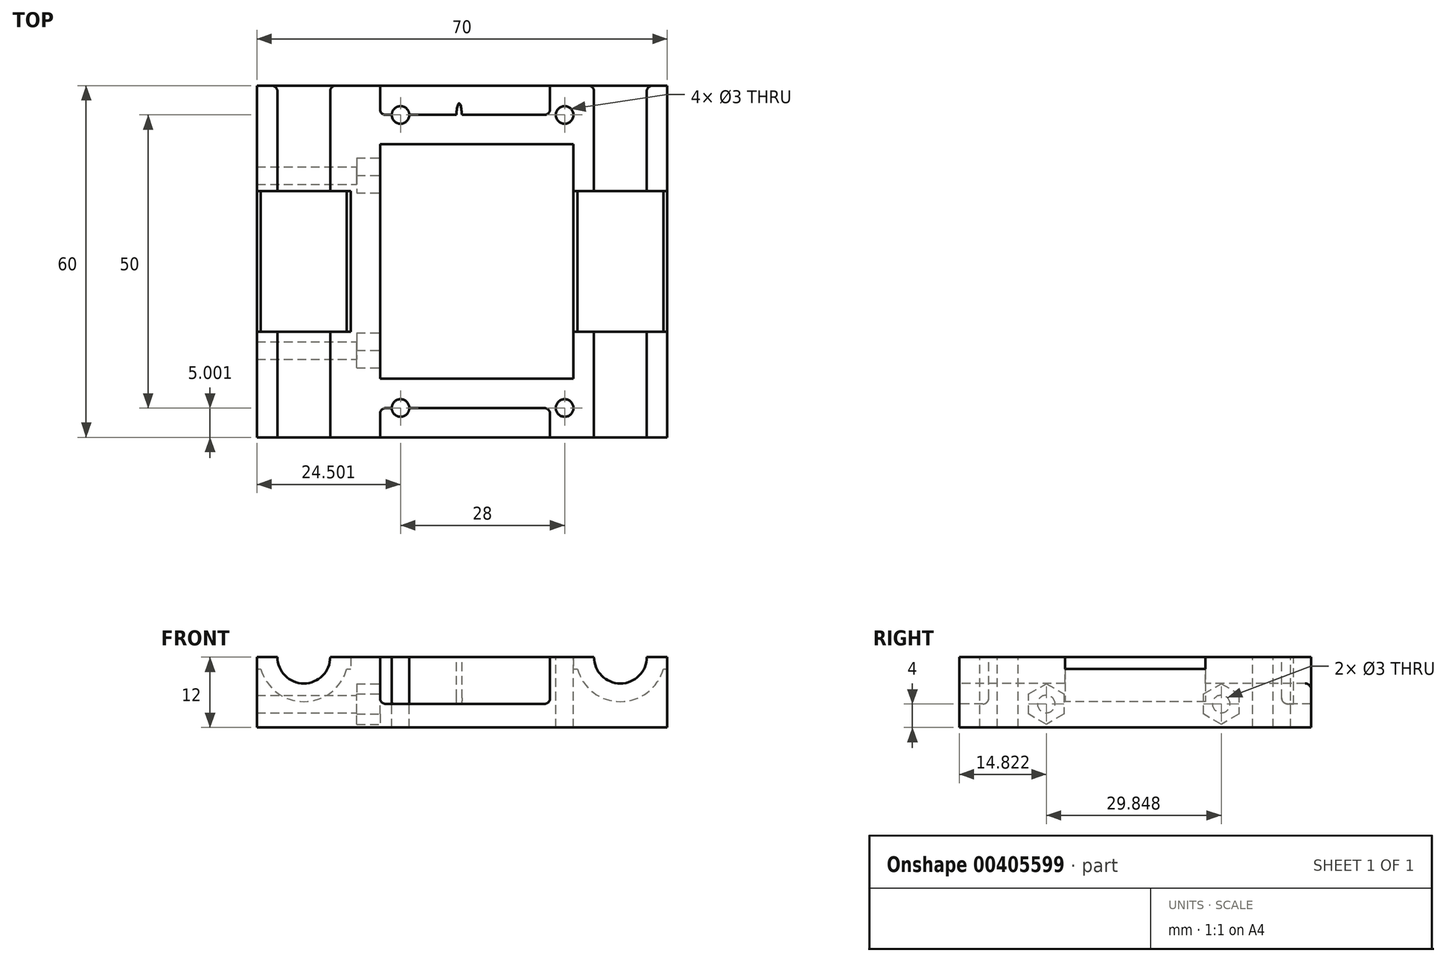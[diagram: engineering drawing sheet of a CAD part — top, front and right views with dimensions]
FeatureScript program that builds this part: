
annotation { "Feature Type Name" : "Feature", "Feature Type Description" : "" }
export const myFeature = defineFeature(function(context is Context, id is Id, definition is map)
    precondition{}
    {
        {
            var Q0;
            Q0=qCreatedBy(makeId("Top.planeOp"),FACE);
            var sketch = newSketch(context, id + "F0", { "sketchPlane" : qUnion([Q0])});
            skLineSegment(sketch, "E0.bottom", {"start": v(-70.16, 26.77) * mm, "end": v(-0.16, 26.77) * mm});
            skLineSegment(sketch, "E0.top", {"start": v(-70.16, -33.23) * mm, "end": v(-0.16, -33.23) * mm});
            skLineSegment(sketch, "E0.left", {"start": v(-70.16, 26.77) * mm, "end": v(-70.16, -33.23) * mm});
            skLineSegment(sketch, "E0.right", {"start": v(-0.16, 26.77) * mm, "end": v(-0.16, -33.23) * mm});
            skSolve(sketch);
        }
        {
            var Q0;
            Q0=qSketchRegion(id+"F0",true);
            extrude(context, id + "F1", {"entities" : qUnion([Q0]), "depth" : 12 * mm});
        }
        {
            var Q0;
            Q0=makeQuery(id+"F1.opExtrude","SWEPT_FACE",FACE,{"disambiguationData":[OSD([sQuery(id+"F0.wireOp",EDGE,"E0.top")])]});
            var sketch = newSketch(context, id + "F2", { "sketchPlane" : qUnion([Q0])});
            skCircle(sketch, "E1", {"center": v(-62.16, 12) * mm, "radius": 7.6 * mm});
            skCircle(sketch, "E2", {"center": v(-8.16, 12) * mm, "radius": 7.6 * mm});
            skLineSegment(sketch, "E3", {"start": v(-72.33, 10) * mm, "end": v(-69.5, 10) * mm});
            skLineSegment(sketch, "E4.trimOffspring", {"start": v(-0.83, 10) * mm, "end": v(3.14, 10) * mm});
            skLineSegment(sketch, "E5", {"start": v(-54.83, 10) * mm, "end": v(-53.13, 10) * mm});
            skLineSegment(sketch, "E6", {"start": v(-53.13, 10) * mm, "end": v(-15.5, 10) * mm});
            skLineSegment(sketch, "E7", {"start": v(-54.16, 12.88) * mm, "end": v(-54.16, 8) * mm});
            skLineSegment(sketch, "E8", {"start": v(-16.16, 15.66) * mm, "end": v(-16.16, -2.6) * mm});
            skCircle(sketch, "E9", {"center": v(-62.16, 12) * mm, "radius": 4.5 * mm});
            skCircle(sketch, "E10", {"center": v(-8.16, 12) * mm, "radius": 4.5 * mm});
            skSolve(sketch);
        }
        {
            var Q0;
            {var subQ0=sQuery(id+"F2.wireOp",EDGE,"E2");var subQ1=makeQuery(id+"F2.imprint","INTERSECT",VERTEX,{"derivedFrom":[subQ0,sQuery(id+"F2.wireOp",EDGE,"E4.trimOffspring")]});Q0=makeQuery(id+"F2.imprint","IMPRINT",FACE,{"disambiguationData":[TD([[makeQuery(id+"F2.imprint","IMPRINT",EDGE,{"disambiguationData":[TD([[subQ1,1.0]])],"derivedFrom":subQ0}),1.0]])]});}
            var Q1;
            {var subQ0=sQuery(id+"F2.wireOp",EDGE,"E1");var subQ1=makeQuery(id+"F2.imprint","INTERSECT",VERTEX,{"derivedFrom":[subQ0,sQuery(id+"F2.wireOp",EDGE,"E3")]});Q1=makeQuery(id+"F2.imprint","IMPRINT",FACE,{"disambiguationData":[TD([[makeQuery(id+"F2.imprint","IMPRINT",EDGE,{"disambiguationData":[TD([[subQ1,1.0]])],"derivedFrom":subQ0}),1.0]])]});}
            var Q2;
            {var subQ0=sQuery(id+"F2.wireOp",EDGE,"E4.trimOffspring");var subQ1=sQuery(id+"F2.wireOp",EDGE,"E2");var subQ2=makeQuery(id+"F2.imprint","INTERSECT",VERTEX,{"derivedFrom":[subQ1,subQ0]});Q2=makeQuery(id+"F2.imprint","IMPRINT",FACE,{"disambiguationData":[TD([[makeQuery(id+"F2.imprint","IMPRINT",EDGE,{"disambiguationData":[TD([[subQ2,-1.0]])],"derivedFrom":subQ1}),-1.0]])]});}
            var Q3;
            {var subQ0=sQuery(id+"F2.wireOp",EDGE,"E3");var subQ1=sQuery(id+"F2.wireOp",EDGE,"E1");var subQ2=makeQuery(id+"F2.imprint","INTERSECT",VERTEX,{"derivedFrom":[subQ1,subQ0]});Q3=makeQuery(id+"F2.imprint","IMPRINT",FACE,{"disambiguationData":[TD([[makeQuery(id+"F2.imprint","IMPRINT",EDGE,{"disambiguationData":[TD([[subQ2,1.0]])],"derivedFrom":subQ1}),-1.0]])]});}
            var Q4;
            {var subQ0=sQuery(id+"F2.wireOp",EDGE,"E6");var subQ1=sQuery(id+"F2.wireOp",EDGE,"E2");var subQ2=makeQuery(id+"F2.imprint","INTERSECT",VERTEX,{"derivedFrom":[subQ1,subQ0]});Q4=makeQuery(id+"F2.imprint","IMPRINT",FACE,{"disambiguationData":[TD([[makeQuery(id+"F2.imprint","IMPRINT",EDGE,{"disambiguationData":[TD([[subQ2,1.0]])],"derivedFrom":subQ1}),-1.0]])]});}
            var Q5;
            {var subQ0=sQuery(id+"F2.wireOp",EDGE,"E5");var subQ1=sQuery(id+"F2.wireOp",EDGE,"E1");var subQ2=makeQuery(id+"F2.imprint","INTERSECT",VERTEX,{"derivedFrom":[subQ1,subQ0]});Q5=makeQuery(id+"F2.imprint","IMPRINT",FACE,{"disambiguationData":[TD([[makeQuery(id+"F2.imprint","IMPRINT",EDGE,{"disambiguationData":[TD([[subQ2,-1.0]])],"derivedFrom":subQ1}),-1.0]])]});}
            extrude(context, id + "F3", {"entities" : qUnion([Q0, Q1, Q2, Q3, Q4, Q5]), "operationType" : NewBodyOperationType.REMOVE, "oppositeDirection" : true, "depth" : 42 * mm});
        }
        {
            var Q0;
            {var subQ0=sQuery(id+"F2.wireOp",EDGE,"E3");var subQ1=sQuery(id+"F2.wireOp",EDGE,"E1");var subQ2=makeQuery(id+"F2.imprint","INTERSECT",VERTEX,{"derivedFrom":[subQ1,subQ0]});Q0=makeQuery(id+"F2.imprint","IMPRINT",FACE,{"disambiguationData":[TD([[makeQuery(id+"F2.imprint","IMPRINT",EDGE,{"disambiguationData":[TD([[subQ2,1.0]])],"derivedFrom":subQ1}),-1.0]])]});}
            var Q1;
            {var subQ0=sQuery(id+"F2.wireOp",EDGE,"E1");var subQ1=makeQuery(id+"F2.imprint","INTERSECT",VERTEX,{"derivedFrom":[subQ0,sQuery(id+"F2.wireOp",EDGE,"E3")]});Q1=makeQuery(id+"F2.imprint","IMPRINT",FACE,{"disambiguationData":[TD([[makeQuery(id+"F2.imprint","IMPRINT",EDGE,{"disambiguationData":[TD([[subQ1,1.0]])],"derivedFrom":subQ0}),1.0]])]});}
            var Q2;
            {var subQ0=sQuery(id+"F2.wireOp",EDGE,"E4.trimOffspring");var subQ1=sQuery(id+"F2.wireOp",EDGE,"E2");var subQ2=makeQuery(id+"F2.imprint","INTERSECT",VERTEX,{"derivedFrom":[subQ1,subQ0]});Q2=makeQuery(id+"F2.imprint","IMPRINT",FACE,{"disambiguationData":[TD([[makeQuery(id+"F2.imprint","IMPRINT",EDGE,{"disambiguationData":[TD([[subQ2,-1.0]])],"derivedFrom":subQ1}),-1.0]])]});}
            var Q3;
            {var subQ0=sQuery(id+"F2.wireOp",EDGE,"E5");var subQ1=sQuery(id+"F2.wireOp",EDGE,"E1");var subQ2=makeQuery(id+"F2.imprint","INTERSECT",VERTEX,{"derivedFrom":[subQ1,subQ0]});Q3=makeQuery(id+"F2.imprint","IMPRINT",FACE,{"disambiguationData":[TD([[makeQuery(id+"F2.imprint","IMPRINT",EDGE,{"disambiguationData":[TD([[subQ2,-1.0]])],"derivedFrom":subQ1}),-1.0]])]});}
            var Q4;
            {var subQ0=sQuery(id+"F2.wireOp",EDGE,"E2");var subQ1=makeQuery(id+"F2.imprint","INTERSECT",VERTEX,{"derivedFrom":[subQ0,sQuery(id+"F2.wireOp",EDGE,"E6")]});Q4=makeQuery(id+"F2.imprint","IMPRINT",FACE,{"disambiguationData":[TD([[makeQuery(id+"F2.imprint","IMPRINT",EDGE,{"disambiguationData":[TD([[subQ1,1.0]])],"derivedFrom":subQ0}),1.0]])]});}
            var Q5;
            {var subQ0=sQuery(id+"F2.wireOp",EDGE,"E6");var subQ1=sQuery(id+"F2.wireOp",EDGE,"E2");var subQ2=makeQuery(id+"F2.imprint","INTERSECT",VERTEX,{"derivedFrom":[subQ1,subQ0]});Q5=makeQuery(id+"F2.imprint","IMPRINT",FACE,{"disambiguationData":[TD([[makeQuery(id+"F2.imprint","IMPRINT",EDGE,{"disambiguationData":[TD([[subQ2,1.0]])],"derivedFrom":subQ1}),-1.0]])]});}
            extrude(context, id + "F4", {"entities" : qUnion([Q0, Q1, Q2, Q3, Q4, Q5]), "operationType" : NewBodyOperationType.ADD, "oppositeDirection" : true, "depth" : 18 * mm});
        }
        {
            var Q0;
            {var subQ0=sQuery(id+"F2.wireOp",EDGE,"E2");var subQ1=sQuery(id+"F0.wireOp",EDGE,"E0.top");var subQ2=makeQuery(id+"F1.opExtrude","CAP_EDGE",EDGE,{"disambiguationData":[OSD([subQ1])],"isStart":false});var subQ3=makeQuery(id+"F2.imprint","INTERSECT",VERTEX,{"disambiguationData":[OD(1.0)],"derivedFrom":[subQ2,subQ0]});var subQ4=sQuery(id+"F0.wireOp",EDGE,"E0.right");var subQ5=sQuery(id+"F2.wireOp",EDGE,"E1");var subQ6=makeQuery(id+"F2.imprint","INTERSECT",VERTEX,{"disambiguationData":[OD(0.0)],"derivedFrom":[subQ2,subQ5]});var subQ7=sQuery(id+"F0.wireOp",EDGE,"E0.left");Q0=makeQuery(id+"F4.boolean.opBoolean","MERGE",FACE,{"derivedFrom":[makeQuery(id+"F1.opExtrude","CAP_FACE",FACE,{"disambiguationData":[OSD([sQuery(id+"F0.wireOp",EDGE,"E0.bottom"),subQ1,subQ7,subQ4])],"isStart":false}),makeQuery(id+"F4.opExtrude","SWEPT_FACE",FACE,{"disambiguationData":[OSD([subQ1]),TDD([makeQuery(id+"F2.imprint","IMPRINT",EDGE,{"disambiguationData":[TD([[subQ6,1.0]])],"derivedFrom":subQ2}),makeQuery(id+"F2.imprint","IMPRINT",EDGE,{"disambiguationData":[TD([[subQ6,-1.0]])],"derivedFrom":subQ2})])]}),makeQuery(id+"F4.opExtrude","SWEPT_FACE",FACE,{"disambiguationData":[OSD([subQ1]),TDD([makeQuery(id+"F2.imprint","IMPRINT",EDGE,{"disambiguationData":[TD([[subQ3,-1.0]])],"derivedFrom":subQ2}),makeQuery(id+"F2.imprint","IMPRINT",EDGE,{"disambiguationData":[TD([[makeQuery(id+"F2.imprint","INTERSECT",VERTEX,{"disambiguationData":[OD(0.0)],"derivedFrom":[subQ2,subQ0]}),-1.0]])],"derivedFrom":subQ2})])]})]});}
            var sketch = newSketch(context, id + "F5", { "sketchPlane" : qUnion([Q0])});
            skLineSegment(sketch, "E11.bottom", {"start": v(-16.16, -23.23) * mm, "end": v(-49.16, -23.23) * mm});
            skLineSegment(sketch, "E11.top", {"start": v(-16.16, 16.77) * mm, "end": v(-49.16, 16.77) * mm});
            skLineSegment(sketch, "E11.left", {"start": v(-16.16, -23.23) * mm, "end": v(-16.16, 16.77) * mm});
            skPoint(sketch, "E11.middle", {"position": v(-35.16, -3.23) * mm});
            skPoint(sketch, "E11.middle.positionSnap0", {"position": v(-35.16, -33.23) * mm});
            skPoint(sketch, "E11.centerSnap0", {"position": v(-35.16, -33.23) * mm});
            skCircle(sketch, "E12", {"center": v(-45.16, 21.77) * mm, "radius": 1.77 * mm});
            skCircle(sketch, "E13", {"center": v(-17.16, 21.77) * mm, "radius": 1.92 * mm});
            skCircle(sketch, "E14", {"center": v(-45.16, -28.23) * mm, "radius": 1.72 * mm});
            skCircle(sketch, "E15", {"center": v(-17.16, -28.23) * mm, "radius": 1.92 * mm});
            skLineSegment(sketch, "E16.right", {"start": v(-49.16, 26.77) * mm, "end": v(-49.16, -33.23) * mm});
            skLineSegment(sketch, "E17", {"start": v(-55.16, 26.77) * mm, "end": v(-55.16, -33.23) * mm});
            skLineSegment(sketch, "E18", {"start": v(-50.16, 26.77) * mm, "end": v(-50.16, -33.23) * mm});
            skSolve(sketch);
        }
        {
            var Q0;
            Q0=makeQuery(id+"F5.imprint","IMPRINT",FACE,{"disambiguationData":[TD([[makeQuery(id+"F5.imprint","IMPRINT",EDGE,{"derivedFrom":sQuery(id+"F5.wireOp",EDGE,"E11.bottom")}),-1.0]])]});
            extrude(context, id + "F6", {"entities" : qUnion([Q0]), "operationType" : NewBodyOperationType.REMOVE, "oppositeDirection" : true, "depth" : 25 * mm});
        }
        {
            var Q0;
            {var subQ0=sQuery(id+"F2.wireOp",EDGE,"E9");var subQ1=makeQuery(id+"F1.opExtrude","CAP_EDGE",EDGE,{"disambiguationData":[OSD([sQuery(id+"F0.wireOp",EDGE,"E0.top")])],"isStart":false});var subQ2=makeQuery(id+"F2.imprint","INTERSECT",VERTEX,{"disambiguationData":[OD(0.0)],"derivedFrom":[subQ1,subQ0]});Q0=makeQuery(id+"F2.imprint","IMPRINT",FACE,{"disambiguationData":[TD([[makeQuery(id+"F2.imprint","IMPRINT",EDGE,{"disambiguationData":[TD([[subQ2,1.0]])],"derivedFrom":subQ0}),1.0]])]});}
            var Q1;
            {var subQ0=sQuery(id+"F2.wireOp",EDGE,"E9");var subQ1=makeQuery(id+"F1.opExtrude","CAP_EDGE",EDGE,{"disambiguationData":[OSD([sQuery(id+"F0.wireOp",EDGE,"E0.top")])],"isStart":false});var subQ2=makeQuery(id+"F2.imprint","INTERSECT",VERTEX,{"disambiguationData":[OD(0.0)],"derivedFrom":[subQ1,subQ0]});Q1=makeQuery(id+"F2.imprint","IMPRINT",FACE,{"disambiguationData":[TD([[makeQuery(id+"F2.imprint","IMPRINT",EDGE,{"disambiguationData":[TD([[subQ2,-1.0]])],"derivedFrom":subQ0}),1.0]])]});}
            var Q2;
            {var subQ0=sQuery(id+"F2.wireOp",EDGE,"E10");var subQ1=makeQuery(id+"F1.opExtrude","CAP_EDGE",EDGE,{"disambiguationData":[OSD([sQuery(id+"F0.wireOp",EDGE,"E0.top")])],"isStart":false});var subQ2=makeQuery(id+"F2.imprint","INTERSECT",VERTEX,{"disambiguationData":[OD(0.0)],"derivedFrom":[subQ1,subQ0]});Q2=makeQuery(id+"F2.imprint","IMPRINT",FACE,{"disambiguationData":[TD([[makeQuery(id+"F2.imprint","IMPRINT",EDGE,{"disambiguationData":[TD([[subQ2,1.0]])],"derivedFrom":subQ0}),1.0]])]});}
            var Q3;
            {var subQ0=sQuery(id+"F2.wireOp",EDGE,"E10");var subQ1=makeQuery(id+"F1.opExtrude","CAP_EDGE",EDGE,{"disambiguationData":[OSD([sQuery(id+"F0.wireOp",EDGE,"E0.top")])],"isStart":false});var subQ2=makeQuery(id+"F2.imprint","INTERSECT",VERTEX,{"disambiguationData":[OD(0.0)],"derivedFrom":[subQ1,subQ0]});Q3=makeQuery(id+"F2.imprint","IMPRINT",FACE,{"disambiguationData":[TD([[makeQuery(id+"F2.imprint","IMPRINT",EDGE,{"disambiguationData":[TD([[subQ2,-1.0]])],"derivedFrom":subQ0}),1.0]])]});}
            extrude(context, id + "F7", {"entities" : qUnion([Q0, Q1, Q2, Q3]), "operationType" : NewBodyOperationType.REMOVE, "endBound" : BoundingType.THROUGH_ALL, "oppositeDirection" : true, "depth" : 25 * mm});
        }
        {
            var Q0;
            {var subQ0=sQuery(id+"F2.wireOp",EDGE,"E10");var subQ1=sQuery(id+"F2.wireOp",EDGE,"E8");var subQ2=sQuery(id+"F2.wireOp",EDGE,"E6");var subQ3=sQuery(id+"F2.wireOp",EDGE,"E4.trimOffspring");var subQ4=sQuery(id+"F2.wireOp",EDGE,"E2");var subQ5=sQuery(id+"F0.wireOp",EDGE,"E0.right");var subQ6=sQuery(id+"F0.wireOp",EDGE,"E0.top");var subQ7=makeQuery(id+"F4.opExtrude","CAP_FACE",FACE,{"disambiguationData":[OSD([subQ6,subQ5,subQ4,subQ3,subQ2,subQ1,subQ0])],"isStart":false});var subQ8=makeQuery(id+"F1.opExtrude","SWEPT_FACE",FACE,{"disambiguationData":[OSD([subQ6])]});var subQ9=makeQuery(id+"F4.opExtrude","CAP_FACE",FACE,{"disambiguationData":[OSD([subQ6,subQ5,subQ4,subQ3,subQ2,subQ1,subQ0])],"isStart":true});var subQ10=sQuery(id+"F0.wireOp",EDGE,"E0.left");var subQ11=makeQuery(id+"F1.opExtrude","CAP_FACE",FACE,{"disambiguationData":[OSD([sQuery(id+"F0.wireOp",EDGE,"E0.bottom"),subQ6,subQ10,subQ5])],"isStart":false});var subQ12=sQuery(id+"F2.wireOp",EDGE,"E9");var subQ13=sQuery(id+"F2.wireOp",EDGE,"E7");var subQ14=sQuery(id+"F2.wireOp",EDGE,"E5");var subQ15=sQuery(id+"F2.wireOp",EDGE,"E3");var subQ16=sQuery(id+"F2.wireOp",EDGE,"E1");var subQ17=makeQuery(id+"F4.opExtrude","CAP_FACE",FACE,{"disambiguationData":[OSD([subQ6,subQ10,subQ16,subQ15,subQ14,subQ13,subQ12])],"isStart":true});var subQ18=makeQuery(id+"F1.opExtrude","CAP_EDGE",EDGE,{"disambiguationData":[OSD([subQ6])],"isStart":false});var subQ19=makeQuery(id+"F2.imprint","INTERSECT",VERTEX,{"disambiguationData":[OD(0.0)],"derivedFrom":[subQ18,subQ16]});var subQ20=makeQuery(id+"F2.imprint","IMPRINT",EDGE,{"disambiguationData":[TD([[subQ19,-1.0]])],"derivedFrom":subQ18});var subQ21=makeQuery(id+"F2.imprint","IMPRINT",EDGE,{"disambiguationData":[TD([[subQ19,1.0]])],"derivedFrom":subQ18});var subQ22=makeQuery(id+"F4.opExtrude","SWEPT_FACE",FACE,{"disambiguationData":[OSD([subQ6]),TDD([subQ21,subQ20])]});var subQ23=makeQuery(id+"F2.imprint","INTERSECT",VERTEX,{"disambiguationData":[OD(1.0)],"derivedFrom":[subQ18,subQ4]});var subQ24=makeQuery(id+"F2.imprint","IMPRINT",EDGE,{"disambiguationData":[TD([[subQ23,1.0]])],"derivedFrom":subQ18});var subQ25=makeQuery(id+"F2.imprint","IMPRINT",EDGE,{"disambiguationData":[TD([[subQ23,-1.0]])],"derivedFrom":subQ18});var subQ26=makeQuery(id+"F4.opExtrude","SWEPT_FACE",FACE,{"disambiguationData":[OSD([subQ6]),TDD([subQ25,subQ24])]});var subQ27=makeQuery(id+"F2.imprint","INTERSECT",VERTEX,{"disambiguationData":[OD(1.0)],"derivedFrom":[subQ18,subQ16]});var subQ28=makeQuery(id+"F2.imprint","IMPRINT",EDGE,{"disambiguationData":[TD([[subQ27,1.0]])],"derivedFrom":subQ18});var subQ29=makeQuery(id+"F2.imprint","IMPRINT",EDGE,{"disambiguationData":[TD([[makeQuery(id+"F2.imprint","INTERSECT",VERTEX,{"derivedFrom":[subQ18,subQ13]}),1.0]])],"derivedFrom":subQ18});var subQ30=makeQuery(id+"F4.opExtrude","SWEPT_FACE",FACE,{"disambiguationData":[OSD([subQ6]),TDD([subQ29,subQ28])]});var subQ31=makeQuery(id+"F2.imprint","INTERSECT",VERTEX,{"disambiguationData":[OD(0.0)],"derivedFrom":[subQ18,subQ4]});var subQ32=makeQuery(id+"F2.imprint","IMPRINT",EDGE,{"disambiguationData":[TD([[subQ31,-1.0]])],"derivedFrom":subQ18});var subQ33=makeQuery(id+"F2.imprint","IMPRINT",EDGE,{"disambiguationData":[TD([[makeQuery(id+"F2.imprint","INTERSECT",VERTEX,{"derivedFrom":[subQ18,subQ1]}),-1.0]])],"derivedFrom":subQ18});var subQ34=makeQuery(id+"F4.opExtrude","SWEPT_FACE",FACE,{"disambiguationData":[OSD([subQ6]),TDD([subQ33,subQ32])]});var subQ35=makeQuery(id+"F7.opExtrude","SWEPT_FACE",FACE,{"disambiguationData":[OSD([subQ0])]});var subQ36=sQuery(id+"F5.wireOp",EDGE,"E11.bottom");var subQ37=makeQuery(id+"F6.boolean.opBoolean","COPY",FACE,{"derivedFrom":makeQuery(id+"F6.opExtrude","SWEPT_FACE",FACE,{"disambiguationData":[OSD([subQ36])]})});var subQ38=makeQuery(id+"F6.boolean.opBoolean","COPY",FACE,{"derivedFrom":makeQuery(id+"F6.opExtrude","SWEPT_FACE",FACE,{"disambiguationData":[OSD([sQuery(id+"F5.wireOp",EDGE,"E11.left")])]})});Q0=makeQuery(id+"FtBxvbWRXRIYLMa_1.boolean.opBoolean","SPLIT",FACE,{"disambiguationData":[TD([subQ37])],"derivedFrom":makeQuery(id+"F7.boolean.opBoolean","SPLIT",FACE,{"disambiguationData":[TD([subQ8,subQ17,makeQuery(id+"F4.opExtrude","CAP_FACE",FACE,{"disambiguationData":[OSD([subQ6,subQ10,subQ16,subQ15,subQ14,subQ13,subQ12])],"isStart":false}),subQ9,subQ7,subQ37,subQ38,makeQuery(id+"F6.boolean.opBoolean","COPY",FACE,{"derivedFrom":makeQuery(id+"F6.opExtrude","SWEPT_FACE",FACE,{"disambiguationData":[OSD([sQuery(id+"F5.wireOp",EDGE,"E16.left")])]})}),makeQuery(id+"F7.opExtrude","SWEPT_FACE",FACE,{"disambiguationData":[OSD([subQ12])]}),subQ35])],"derivedFrom":makeQuery(id+"F4.boolean.opBoolean","MERGE",FACE,{"derivedFrom":[subQ11,subQ22,subQ26,subQ30,subQ34]})})});}
            var sketch = newSketch(context, id + "F8", { "sketchPlane" : qUnion([Q0])});
            skLineSegment(sketch, "E19.bottom", {"start": v(-40.16, -27.23) * mm, "end": v(-26.16, -27.23) * mm});
            skLineSegment(sketch, "E19.top", {"start": v(-40.16, -33.23) * mm, "end": v(-26.16, -33.23) * mm});
            skLineSegment(sketch, "E20", {"start": v(-40.16, -27.23) * mm, "end": v(-40.16, -27.23) * mm});
            skLineSegment(sketch, "E21", {"start": v(-38.16, -27.23) * mm, "end": v(-37.16, -27.23) * mm});
            skLineSegment(sketch, "E22", {"start": v(-36.16, -27.23) * mm, "end": v(-35.16, -27.23) * mm});
            skLineSegment(sketch, "E23", {"start": v(-35.16, -27.23) * mm, "end": v(-34.16, -27.23) * mm});
            skLineSegment(sketch, "E24", {"start": v(-33.16, -27.23) * mm, "end": v(-32.16, -27.23) * mm});
            skLineSegment(sketch, "E25", {"start": v(-31.16, -27.23) * mm, "end": v(-30.16, -27.23) * mm});
            skLineSegment(sketch, "E26", {"start": v(-29.16, -27.23) * mm, "end": v(-28.16, -27.23) * mm});
            skLineSegment(sketch, "E27", {"start": v(-27.16, -27.23) * mm, "end": v(-26.16, -27.23) * mm});
            skLineSegment(sketch, "E28", {"start": v(-40.13, -28.23) * mm, "end": v(-27.19, -28.23) * mm});
            skLineSegment(sketch, "E29", {"start": v(-40.16, -23.23) * mm, "end": v(-40.16, -27.23) * mm});
            skLineSegment(sketch, "E30.trimOffspring", {"start": v(-40.16, -31.23) * mm, "end": v(-40.16, -33.23) * mm});
            skLineSegment(sketch, "E31", {"start": v(-40.16, -31.23) * mm, "end": v(-26.16, -31.23) * mm});
            skLineSegment(sketch, "E32.top", {"start": v(-26.16, -27.23) * mm, "end": v(-20.16, -27.23) * mm});
            skLineSegment(sketch, "E33.trimOffspring", {"start": v(-26.16, -31.23) * mm, "end": v(-26.16, -33.23) * mm});
            skLineSegment(sketch, "E34", {"start": v(-16.16, -23.23) * mm, "end": v(-16.16, 16.77) * mm});
            skPoint(sketch, "E34.endSnap0", {"position": v(-16.16, -19.23) * mm});
            skLineSegment(sketch, "E35", {"start": v(-16.16, -3.23) * mm, "end": v(-49.15, -3.23) * mm});
            skLineSegment(sketch, "E36.MirrorCS", {"start": v(-16.16, 16.77) * mm, "end": v(-16.16, -23.23) * mm});
            skPoint(sketch, "E37.MirrorP", {"position": v(-16.16, 12.77) * mm});
            skLineSegment(sketch, "E38.MirrorCS", {"start": v(-36.16, 20.77) * mm, "end": v(-35.16, 20.77) * mm});
            skLineSegment(sketch, "E39.MirrorCS", {"start": v(-35.16, 20.77) * mm, "end": v(-34.16, 20.77) * mm});
            skLineSegment(sketch, "E40.MirrorCS", {"start": v(-38.16, 20.77) * mm, "end": v(-37.16, 20.77) * mm});
            skLineSegment(sketch, "E41.MirrorCS", {"start": v(-29.16, 20.77) * mm, "end": v(-28.16, 20.77) * mm});
            skLineSegment(sketch, "E42.MirrorCS", {"start": v(-40.16, 24.77) * mm, "end": v(-40.16, 26.77) * mm});
            skLineSegment(sketch, "E43.MirrorCS", {"start": v(-31.16, 20.77) * mm, "end": v(-30.16, 20.77) * mm});
            skLineSegment(sketch, "E44.MirrorCS", {"start": v(-27.16, 20.77) * mm, "end": v(-26.16, 20.77) * mm});
            skLineSegment(sketch, "E45.MirrorCS", {"start": v(-40.16, 20.77) * mm, "end": v(-26.16, 20.77) * mm});
            skLineSegment(sketch, "E46.MirrorCS", {"start": v(-40.13, 21.77) * mm, "end": v(-27.19, 21.77) * mm});
            skEllipticalArc(sketch, "E47.MirrorCS", {});
            skLineSegment(sketch, "E48.MirrorCS", {"start": v(-33.16, 20.77) * mm, "end": v(-32.16, 20.77) * mm});
            skEllipticalArc(sketch, "E49.MirrorCS", {});
            skLineSegment(sketch, "E50.MirrorCS", {"start": v(-26.16, 24.77) * mm, "end": v(-26.16, 26.77) * mm});
            skLineSegment(sketch, "E51.MirrorCS", {"start": v(-40.16, 24.77) * mm, "end": v(-26.16, 24.77) * mm});
            skLineSegment(sketch, "E52.MirrorCS", {"start": v(-40.16, 26.77) * mm, "end": v(-26.16, 26.77) * mm});
            skEllipticalArc(sketch, "E53.MirrorCS", {});
            skLineSegment(sketch, "E54.MirrorCS", {"start": v(-26.16, 20.77) * mm, "end": v(-17.16, 20.77) * mm});
            skLineSegment(sketch, "E55.MirrorCS", {"start": v(-40.16, 16.77) * mm, "end": v(-40.16, 20.77) * mm});
            skEllipticalArc(sketch, "E56.MirrorCS", {});
            skEllipticalArc(sketch, "E57.MirrorCS", {});
            skEllipticalArc(sketch, "E58.MirrorCS", {});
            skEllipticalArc(sketch, "E59.MirrorCS", {});
            skLineSegment(sketch, "E60", {"start": v(-40.16, 26.77) * mm, "end": v(-49.16, 26.77) * mm});
            skLineSegment(sketch, "E61", {"start": v(-49.16, 26.77) * mm, "end": v(-49.16, 16.77) * mm});
            skLineSegment(sketch, "E62", {"start": v(-49.16, 16.77) * mm, "end": v(-40.16, 16.77) * mm});
            skLineSegment(sketch, "E63", {"start": v(-17.16, 26.77) * mm, "end": v(-26.16, 26.77) * mm});
            skCircle(sketch, "E64", {"center": v(-45.66, -28.23) * mm, "radius": 1.5 * mm});
            skCircle(sketch, "E65", {"center": v(-17.66, -28.23) * mm, "radius": 1.5 * mm});
            skLineSegment(sketch, "E66", {"start": v(-20.16, -27.23) * mm, "end": v(-20.16, -33.23) * mm});
            skPoint(sketch, "E67.orphan", {"position": v(-17.16, -27.23) * mm});
            skCircle(sketch, "E68.MirrorC", {"center": v(-17.66, 21.77) * mm, "radius": 1.5 * mm});
            skLineSegment(sketch, "E69.MirrorCS", {"start": v(-20.16, 20.77) * mm, "end": v(-20.16, 26.77) * mm});
            skCircle(sketch, "E70.MirrorC", {"center": v(-45.66, 21.77) * mm, "radius": 1.5 * mm});
            skLineSegment(sketch, "E71.bottom", {"start": v(-40.16, -27.23) * mm, "end": v(-20.16, -27.23) * mm});
            skLineSegment(sketch, "E71.top", {"start": v(-40.16, -28.23) * mm, "end": v(-20.16, -28.23) * mm});
            skLineSegment(sketch, "E71.left", {"start": v(-40.16, -27.23) * mm, "end": v(-40.16, -28.23) * mm});
            skLineSegment(sketch, "E71.right", {"start": v(-20.16, -27.23) * mm, "end": v(-20.16, -28.23) * mm});
            skLineSegment(sketch, "E72", {"start": v(-27.19, 21.77) * mm, "end": v(-20.16, 21.77) * mm});
            skLineSegment(sketch, "E73", {"start": v(-40.13, -28.23) * mm, "end": v(-49.16, -28.23) * mm});
            skLineSegment(sketch, "E74", {"start": v(-40.13, 21.77) * mm, "end": v(-49.16, 21.77) * mm});
            skLineSegment(sketch, "E75", {"start": v(-49.16, -28.23) * mm, "end": v(-50.16, -28.23) * mm});
            skLineSegment(sketch, "E76", {"start": v(-49.16, 21.77) * mm, "end": v(-50.16, 21.77) * mm});
            skLineSegment(sketch, "E77", {"start": v(-49.16, 16.77) * mm, "end": v(-49.16, -33.23) * mm});
            const initialGuessF8  = {"E47.MirrorCS": [-0.039659118611365556, 0.020770615064917446, 0, 1, 0.003, 0.0005, 4.71238898038469, 1.5707963267948966], "E49.MirrorCS": [-0.027659118611365545, 0.020770615064917446, 0, 1, 0.003, 0.0005, 4.71238898038469, 1.5707963267948966], "E53.MirrorCS": [-0.037659118611365554, 0.020770615064917446, 0, 1, 0.003, 0.0005, 4.71238898038469, 1.5707963267948966], "E56.MirrorCS": [-0.029659118611365547, 0.020770615064917446, 0, 1, 0.003, 0.0005, 4.71238898038469, 1.5707963267948966], "E57.MirrorCS": [-0.03365911861136555, 0.020770615064917446, 0, 1, 0.003, 0.0005, 4.71238898038469, 1.5707963267948966], "E58.MirrorCS": [-0.03165911861136555, 0.020770615064917446, 0, 1, 0.003, 0.0005, 4.71238898038469, 1.5707963267948966], "E59.MirrorCS": [-0.03565911861136555, 0.020770615064917446, 0, 1, 0.003, 0.0005, 4.71238898038469, 1.5707963267948966]};
            skSetInitialGuess(sketch, initialGuessF8);
            skSolve(sketch);
        }
        {
            var Q0;
            {var subQ40=sQuery(id+"F8.wireOp",EDGE,"E30.trimOffspring");Q0=makeQuery(id+"F8.imprint","IMPRINT",FACE,{"disambiguationData":[TD([[makeQuery(id+"F8.imprint","IMPRINT",EDGE,{"derivedFrom":subQ40}),-1.0]])]});}
            var Q1;
            Q1=makeQuery(id+"F8.imprint","IMPRINT",FACE,{"disambiguationData":[TD([[makeQuery(id+"F8.imprint","IMPRINT",EDGE,{"derivedFrom":sQuery(id+"F8.wireOp",EDGE,"E19.top")}),1.0]])]});
            var Q2;
            {var subQ0=sQuery(id+"F8.wireOp",EDGE,"E47.MirrorCS");var subQ1=sQuery(id+"F8.wireOp",EDGE,"E46.MirrorCS");var subQ2=makeQuery(id+"F8.imprint","INTERSECT",VERTEX,{"disambiguationData":[OD(0.0)],"derivedFrom":[subQ1,subQ0]});Q2=makeQuery(id+"F8.imprint","IMPRINT",FACE,{"disambiguationData":[TD([[makeQuery(id+"F8.imprint","IMPRINT",EDGE,{"disambiguationData":[TD([[subQ2,-1.0]])],"derivedFrom":subQ1}),1.0]])]});}
            var Q3;
            {var subQ0=sQuery(id+"F8.wireOp",EDGE,"E53.MirrorCS");var subQ1=sQuery(id+"F8.wireOp",EDGE,"E46.MirrorCS");var subQ2=makeQuery(id+"F8.imprint","INTERSECT",VERTEX,{"disambiguationData":[OD(0.0)],"derivedFrom":[subQ1,subQ0]});Q3=makeQuery(id+"F8.imprint","IMPRINT",FACE,{"disambiguationData":[TD([[makeQuery(id+"F8.imprint","IMPRINT",EDGE,{"disambiguationData":[TD([[subQ2,-1.0]])],"derivedFrom":subQ1}),1.0]])]});}
            var Q4;
            Q4=makeQuery(id+"F8.imprint","IMPRINT",FACE,{"disambiguationData":[TD([[makeQuery(id+"F8.imprint","IMPRINT",EDGE,{"derivedFrom":sQuery(id+"F8.wireOp",EDGE,"E42.MirrorCS")}),-1.0]])]});
            var Q5;
            {var subQ0=sQuery(id+"F8.wireOp",EDGE,"E59.MirrorCS");var subQ1=sQuery(id+"F8.wireOp",EDGE,"E46.MirrorCS");var subQ2=makeQuery(id+"F8.imprint","INTERSECT",VERTEX,{"disambiguationData":[OD(0.0)],"derivedFrom":[subQ1,subQ0]});Q5=makeQuery(id+"F8.imprint","IMPRINT",FACE,{"disambiguationData":[TD([[makeQuery(id+"F8.imprint","IMPRINT",EDGE,{"disambiguationData":[TD([[subQ2,-1.0]])],"derivedFrom":subQ1}),1.0]])]});}
            var Q6;
            {var subQ0=sQuery(id+"F8.wireOp",EDGE,"E57.MirrorCS");var subQ1=sQuery(id+"F8.wireOp",EDGE,"E46.MirrorCS");var subQ2=makeQuery(id+"F8.imprint","INTERSECT",VERTEX,{"disambiguationData":[OD(0.0)],"derivedFrom":[subQ1,subQ0]});Q6=makeQuery(id+"F8.imprint","IMPRINT",FACE,{"disambiguationData":[TD([[makeQuery(id+"F8.imprint","IMPRINT",EDGE,{"disambiguationData":[TD([[subQ2,-1.0]])],"derivedFrom":subQ1}),1.0]])]});}
            var Q7;
            {var subQ0=sQuery(id+"F8.wireOp",EDGE,"E58.MirrorCS");var subQ1=sQuery(id+"F8.wireOp",EDGE,"E46.MirrorCS");var subQ2=makeQuery(id+"F8.imprint","INTERSECT",VERTEX,{"disambiguationData":[OD(0.0)],"derivedFrom":[subQ1,subQ0]});Q7=makeQuery(id+"F8.imprint","IMPRINT",FACE,{"disambiguationData":[TD([[makeQuery(id+"F8.imprint","IMPRINT",EDGE,{"disambiguationData":[TD([[subQ2,-1.0]])],"derivedFrom":subQ1}),1.0]])]});}
            var Q8;
            {var subQ0=sQuery(id+"F8.wireOp",EDGE,"E56.MirrorCS");var subQ1=sQuery(id+"F8.wireOp",EDGE,"E46.MirrorCS");var subQ2=makeQuery(id+"F8.imprint","INTERSECT",VERTEX,{"disambiguationData":[OD(0.0)],"derivedFrom":[subQ1,subQ0]});Q8=makeQuery(id+"F8.imprint","IMPRINT",FACE,{"disambiguationData":[TD([[makeQuery(id+"F8.imprint","IMPRINT",EDGE,{"disambiguationData":[TD([[subQ2,-1.0]])],"derivedFrom":subQ1}),1.0]])]});}
            var Q9;
            {var subQ0=sQuery(id+"F8.wireOp",EDGE,"E49.MirrorCS");var subQ1=sQuery(id+"F8.wireOp",EDGE,"E46.MirrorCS");var subQ3=makeQuery(id+"F8.imprint","INTERSECT",VERTEX,{"derivedFrom":[subQ1,subQ0]});Q9=makeQuery(id+"F8.imprint","IMPRINT",FACE,{"disambiguationData":[TD([[makeQuery(id+"F8.imprint","IMPRINT",EDGE,{"disambiguationData":[TD([[subQ3,-1.0]])],"derivedFrom":subQ1}),1.0]])]});}
            var Q10;
            Q10=makeQuery(id+"F8.imprint","IMPRINT",FACE,{"disambiguationData":[TD([[makeQuery(id+"F8.imprint","IMPRINT",EDGE,{"derivedFrom":sQuery(id+"F8.wireOp",EDGE,"E42.MirrorCS")}),1.0]])]});
            var Q11;
            {var subQ0=sQuery(id+"F8.wireOp",EDGE,"E47.MirrorCS");var subQ1=sQuery(id+"F8.wireOp",EDGE,"E46.MirrorCS");var subQ3=makeQuery(id+"F8.imprint","INTERSECT",VERTEX,{"derivedFrom":[subQ1,subQ0]});Q11=makeQuery(id+"F8.imprint","IMPRINT",FACE,{"disambiguationData":[TD([[makeQuery(id+"F8.imprint","IMPRINT",EDGE,{"disambiguationData":[TD([[subQ3,1.0]])],"derivedFrom":subQ1}),1.0]])]});}
            var Q12;
            {var subQ25=sQuery(id+"F8.wireOp",EDGE,"E76");Q12=makeQuery(id+"F8.imprint","IMPRINT",FACE,{"disambiguationData":[TD([[makeQuery(id+"F8.imprint","IMPRINT",EDGE,{"derivedFrom":subQ25}),-1.0]])]});}
            extrude(context, id + "F9", {"entities" : qUnion([Q0, Q1, Q2, Q3, Q4, Q5, Q6, Q7, Q8, Q9, Q10, Q11, Q12]), "operationType" : NewBodyOperationType.REMOVE, "oppositeDirection" : true, "depth" : 8 * mm});
        }
        {
            var Q0;
            Q0=sQuery(id+"F8.wireOp",VERTEX,"E70.MirrorC.center");
            var Q1;
            Q1=sQuery(id+"F8.wireOp",VERTEX,"E68.MirrorC.center");
            var Q2;
            Q2=sQuery(id+"F8.wireOp",VERTEX,"E65.center");
            var Q3;
            Q3=sQuery(id+"F8.wireOp",VERTEX,"E64.center");
            var Q4;
            Q4=makeQuery(id+"F1.opExtrude","SWEPT_BODY",BODY,{"disambiguationData":[OSD([sQuery(id+"F0.wireOp",EDGE,"E0.bottom"),sQuery(id+"F0.wireOp",EDGE,"E0.top"),sQuery(id+"F0.wireOp",EDGE,"E0.left"),sQuery(id+"F0.wireOp",EDGE,"E0.right")])]});
            hole(context, id + "F10", {"style" : HoleStyle.SIMPLE, "endStyle" : HoleEndStyle.THROUGH, "holeDiameter" : 3 * mm, "isTappedThrough" : true, "tappedDepth" : 12 * mm, "tapClearance" : 3, "locations" : qUnion([Q0, Q1, Q2, Q3]), "scope" : qUnion([Q4])});
        }
        {
            var Q0;
            Q0=makeQuery(id+"F6.boolean.opBoolean","COPY",FACE,{"derivedFrom":makeQuery(id+"F6.opExtrude","SWEPT_FACE",FACE,{"disambiguationData":[OSD([sQuery(id+"F5.wireOp",EDGE,"E16.right")])]})});
            var sketch = newSketch(context, id + "F11", { "sketchPlane" : qUnion([Q0])});
            skLineSegment(sketch, "E78", {"start": v(-23.23, 4) * mm, "end": v(16.77, 4) * mm});
            skCircle(sketch, "E79.cCircle", {"center": v(-18.4, 4) * mm, "radius": 3 * mm, "construction": true});
            skLineSegment(sketch, "E79.0", {"start": v(-15.4, 5.73) * mm, "end": v(-15.4, 2.27) * mm});
            skLineSegment(sketch, "E79.1", {"start": v(-15.4, 2.27) * mm, "end": v(-18.4, 0.54) * mm});
            skLineSegment(sketch, "E79.2", {"start": v(-18.4, 0.54) * mm, "end": v(-21.4, 2.27) * mm});
            skLineSegment(sketch, "E79.3", {"start": v(-21.4, 2.27) * mm, "end": v(-21.4, 5.73) * mm});
            skLineSegment(sketch, "E79.4", {"start": v(-21.4, 5.73) * mm, "end": v(-18.4, 7.46) * mm});
            skLineSegment(sketch, "E79.5", {"start": v(-18.4, 7.46) * mm, "end": v(-15.4, 5.73) * mm});
            skPoint(sketch, "E79.0.midPoint", {"position": v(-15.4, 4) * mm});
            skCircle(sketch, "E80.cCircle", {"center": v(11.44, 4) * mm, "radius": 3 * mm, "construction": true});
            skLineSegment(sketch, "E80.0", {"start": v(14.44, 5.73) * mm, "end": v(14.44, 2.27) * mm});
            skLineSegment(sketch, "E80.1", {"start": v(14.44, 2.27) * mm, "end": v(11.44, 0.54) * mm});
            skLineSegment(sketch, "E80.2", {"start": v(11.44, 0.54) * mm, "end": v(8.44, 2.27) * mm});
            skLineSegment(sketch, "E80.3", {"start": v(8.44, 2.27) * mm, "end": v(8.44, 5.73) * mm});
            skLineSegment(sketch, "E80.4", {"start": v(8.44, 5.73) * mm, "end": v(11.44, 7.46) * mm});
            skLineSegment(sketch, "E80.5", {"start": v(11.44, 7.46) * mm, "end": v(14.44, 5.73) * mm});
            skPoint(sketch, "E80.0.midPoint", {"position": v(14.44, 4) * mm});
            skSolve(sketch);
        }
        {
            var Q0;
            Q0=qSketchRegion(id+"F11",true);
            extrude(context, id + "F12", {"entities" : qUnion([Q0]), "operationType" : NewBodyOperationType.REMOVE, "oppositeDirection" : true, "depth" : 4 * mm});
        }
        {
            var Q0;
            Q0=sQuery(id+"F11.wireOp",VERTEX,"E79.cCircle.center");
            var Q1;
            Q1=sQuery(id+"F11.wireOp",VERTEX,"E80.cCircle.center");
            var Q2;
            Q2=makeQuery(id+"F1.opExtrude","SWEPT_BODY",BODY,{"disambiguationData":[OSD([sQuery(id+"F0.wireOp",EDGE,"E0.bottom"),sQuery(id+"F0.wireOp",EDGE,"E0.top"),sQuery(id+"F0.wireOp",EDGE,"E0.left"),sQuery(id+"F0.wireOp",EDGE,"E0.right")])]});
            hole(context, id + "F13", {"style" : HoleStyle.SIMPLE, "endStyle" : HoleEndStyle.THROUGH, "holeDiameter" : 3 * mm, "isTappedThrough" : true, "tappedDepth" : 12 * mm, "tapClearance" : 3, "locations" : qUnion([Q0, Q1]), "scope" : qUnion([Q2])});
        }
        {
            var Q0;
            Q0=makeQuery(id+"F1.opExtrude","SWEPT_BODY",BODY,{"disambiguationData":[OSD([sQuery(id+"F0.wireOp",EDGE,"E0.bottom"),sQuery(id+"F0.wireOp",EDGE,"E0.top"),sQuery(id+"F0.wireOp",EDGE,"E0.left"),sQuery(id+"F0.wireOp",EDGE,"E0.right")])]});
            var Q1;
            Q1=qCreatedBy(makeId("Right.planeOp"),FACE);
            mirror(context, id + "F14", {"entities" : qUnion([Q0]), "mirrorPlane" : qUnion([Q1])});
        }
        {
            var Q0;
            Q0=makeQuery(id+"F14.opPattern","COPY",BODY,{"derivedFrom":makeQuery(id+"F1.opExtrude","SWEPT_BODY",BODY,{"disambiguationData":[OSD([sQuery(id+"F0.wireOp",EDGE,"E0.bottom"),sQuery(id+"F0.wireOp",EDGE,"E0.top"),sQuery(id+"F0.wireOp",EDGE,"E0.left"),sQuery(id+"F0.wireOp",EDGE,"E0.right")])]}),"instanceName":"1"});
            deleteBodies(context, id + "F15", {"entities" : qUnion([Q0])});
        }
        {
            var Q0;
            Q0=makeQuery(id+"F7.boolean.opBoolean","INTERSECT",EDGE,{"derivedFrom":[makeQuery(id+"F1.opExtrude","SWEPT_FACE",FACE,{"disambiguationData":[OSD([sQuery(id+"F0.wireOp",EDGE,"E0.bottom")])]}),makeQuery(id+"F7.opExtrude","SWEPT_FACE",FACE,{"disambiguationData":[OSD([sQuery(id+"F2.wireOp",EDGE,"E9")])]})]});
            var Q1;
            Q1=makeQuery(id+"F3.boolean.opBoolean","COPY",EDGE,{"derivedFrom":makeQuery(id+"F3.opExtrude","CAP_EDGE",EDGE,{"disambiguationData":[OSD([sQuery(id+"F2.wireOp",EDGE,"E9")])],"isStart":false})});
            var Q2;
            Q2=makeQuery(id+"F4.opExtrude","CAP_EDGE",EDGE,{"disambiguationData":[OSD([sQuery(id+"F2.wireOp",EDGE,"E9")])],"isStart":false});
            var Q3;
            Q3=makeQuery(id+"F7.boolean.opBoolean","COPY",EDGE,{"derivedFrom":makeQuery(id+"F7.opExtrude","CAP_EDGE",EDGE,{"disambiguationData":[OSD([sQuery(id+"F2.wireOp",EDGE,"E9")])],"isStart":true})});
            var Q4;
            Q4=makeQuery(id+"F7.boolean.opBoolean","COPY",EDGE,{"derivedFrom":makeQuery(id+"F7.opExtrude","CAP_EDGE",EDGE,{"disambiguationData":[OSD([sQuery(id+"F2.wireOp",EDGE,"E10")])],"isStart":true})});
            var Q5;
            Q5=makeQuery(id+"F4.opExtrude","CAP_EDGE",EDGE,{"disambiguationData":[OSD([sQuery(id+"F2.wireOp",EDGE,"E10")])],"isStart":false});
            var Q6;
            Q6=makeQuery(id+"F3.boolean.opBoolean","COPY",EDGE,{"derivedFrom":makeQuery(id+"F3.opExtrude","CAP_EDGE",EDGE,{"disambiguationData":[OSD([sQuery(id+"F2.wireOp",EDGE,"E10")])],"isStart":false})});
            var Q7;
            Q7=makeQuery(id+"F7.boolean.opBoolean","INTERSECT",EDGE,{"derivedFrom":[makeQuery(id+"F1.opExtrude","SWEPT_FACE",FACE,{"disambiguationData":[OSD([sQuery(id+"F0.wireOp",EDGE,"E0.bottom")])]}),makeQuery(id+"F7.opExtrude","SWEPT_FACE",FACE,{"disambiguationData":[OSD([sQuery(id+"F2.wireOp",EDGE,"E10")])]})]});
            var Q8;
            Q8=makeQuery(id+"F9.boolean.opBoolean","COPY",EDGE,{"derivedFrom":makeQuery(id+"F9.opExtrude","CAP_EDGE",EDGE,{"disambiguationData":[OSD([sQuery(id+"F8.wireOp",EDGE,"E46.MirrorCS"),sQuery(id+"F8.wireOp",EDGE,"E72"),sQuery(id+"F8.wireOp",EDGE,"E74")])],"isStart":false})});
            var Q9;
            Q9=makeQuery(id+"F9.boolean.opBoolean","COPY",EDGE,{"derivedFrom":makeQuery(id+"F9.opExtrude","CAP_EDGE",EDGE,{"disambiguationData":[OSD([sQuery(id+"F8.wireOp",EDGE,"E74")])],"isStart":false})});
            var Q10;
            Q10=makeQuery(id+"F9.boolean.opBoolean","COPY",EDGE,{"derivedFrom":makeQuery(id+"F9.opExtrude","CAP_EDGE",EDGE,{"disambiguationData":[OSD([sQuery(id+"F8.wireOp",EDGE,"E71.top"),sQuery(id+"F8.wireOp",EDGE,"E73")])],"isStart":false})});
            var Q11;
            Q11=makeQuery(id+"F9.boolean.opBoolean","COPY",EDGE,{"derivedFrom":makeQuery(id+"F9.opExtrude","CAP_EDGE",EDGE,{"disambiguationData":[OSD([sQuery(id+"F8.wireOp",EDGE,"E73")])],"isStart":false})});
            var Q12;
            Q12=makeQuery(id+"F9.boolean.opBoolean","COPY",EDGE,{"derivedFrom":makeQuery(id+"F9.opExtrude","CAP_EDGE",EDGE,{"disambiguationData":[OSD([sQuery(id+"F8.wireOp",EDGE,"E77")])],"isStart":false})});
            var Q13;
            Q13=makeQuery(id+"F9.boolean.opBoolean","COPY",EDGE,{"derivedFrom":makeQuery(id+"F9.opExtrude","CAP_EDGE",EDGE,{"disambiguationData":[OSD([sQuery(id+"F8.wireOp",EDGE,"E66")])],"isStart":false})});
            var Q14;
            Q14=makeQuery(id+"F9.boolean.opBoolean","COPY",EDGE,{"derivedFrom":makeQuery(id+"F9.opExtrude","CAP_EDGE",EDGE,{"disambiguationData":[OSD([sQuery(id+"F8.wireOp",EDGE,"E61")])],"isStart":false})});
            var Q15;
            Q15=makeQuery(id+"F9.boolean.opBoolean","COPY",EDGE,{"derivedFrom":makeQuery(id+"F9.opExtrude","SWEPT_EDGE",EDGE,{"disambiguationData":[OSD([sQuery(id+"F8.wireOp",EDGE,"E61"),sQuery(id+"F8.wireOp",EDGE,"E74")])]})});
            var Q16;
            Q16=makeQuery(id+"F9.boolean.opBoolean","COPY",EDGE,{"derivedFrom":makeQuery(id+"F9.opExtrude","CAP_EDGE",EDGE,{"disambiguationData":[OSD([sQuery(id+"F8.wireOp",EDGE,"E69.MirrorCS")])],"isStart":false})});
            var Q17;
            Q17=makeQuery(id+"F9.boolean.opBoolean","COPY",EDGE,{"derivedFrom":makeQuery(id+"F9.opExtrude","SWEPT_EDGE",EDGE,{"disambiguationData":[OSD([sQuery(id+"F8.wireOp",EDGE,"E69.MirrorCS"),sQuery(id+"F8.wireOp",EDGE,"E72")])]})});
            var Q18;
            Q18=makeQuery(id+"F9.boolean.opBoolean","COPY",EDGE,{"derivedFrom":makeQuery(id+"F9.opExtrude","SWEPT_EDGE",EDGE,{"disambiguationData":[OSD([sQuery(id+"F8.wireOp",EDGE,"E66"),sQuery(id+"F8.wireOp",EDGE,"E71.top"),sQuery(id+"F8.wireOp",EDGE,"E71.right")])]})});
            var Q19;
            Q19=makeQuery(id+"F9.boolean.opBoolean","COPY",EDGE,{"derivedFrom":makeQuery(id+"F9.opExtrude","SWEPT_EDGE",EDGE,{"disambiguationData":[OSD([sQuery(id+"F8.wireOp",EDGE,"E73"),sQuery(id+"F8.wireOp",EDGE,"E77")])]})});
            fillet(context, id + "F16", {"entities" : qUnion([Q0, Q1, Q2, Q3, Q4, Q5, Q6, Q7, Q8, Q9, Q10, Q11, Q12, Q13, Q14, Q15, Q16, Q17, Q18, Q19]), "radius" : 1 * mm, "tangentPropagation" : true, "allowEdgeOverflow" : false});
        }
    });
